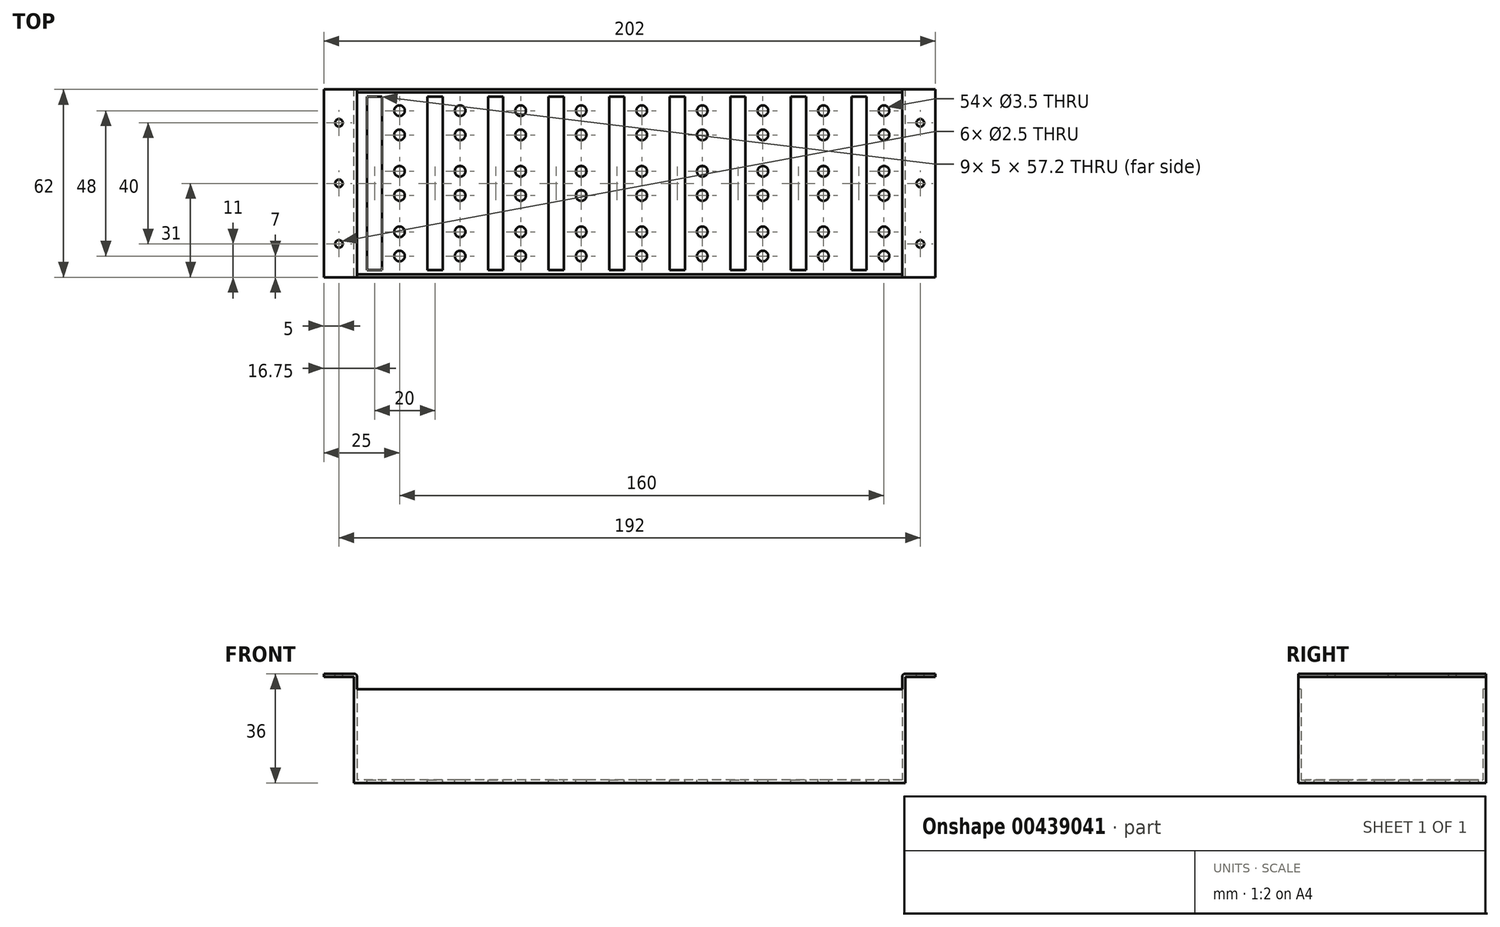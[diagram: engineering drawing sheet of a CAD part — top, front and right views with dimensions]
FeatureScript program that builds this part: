
annotation { "Feature Type Name" : "Feature", "Feature Type Description" : "" }
export const myFeature = defineFeature(function(context is Context, id is Id, definition is map)
    precondition{}
    {
        {
            var Q0;
            Q0=qCreatedBy(makeId("Top.planeOp"),FACE);
            var sketch = newSketch(context, id + "F0", { "sketchPlane" : qUnion([Q0])});
            skLineSegment(sketch, "E0.bottom", {"start": v(91, -31) * mm, "end": v(-91, -31) * mm});
            skLineSegment(sketch, "E0.top", {"start": v(91, 31) * mm, "end": v(-91, 31) * mm});
            skLineSegment(sketch, "E0.left", {"start": v(91, -31) * mm, "end": v(91, 31) * mm});
            skLineSegment(sketch, "E0.right", {"start": v(-91, -31) * mm, "end": v(-91, 31) * mm});
            skPoint(sketch, "E0.middle", {"position": v(0, 0) * mm});
            skSolve(sketch);
        }
        {
            var Q0;
            Q0=qSketchRegion(id+"F0",true);
            extrude(context, id + "F1", {"entities" : qUnion([Q0]), "depth" : 36 * mm});
        }
        {
            var Q0;
            Q0=makeQuery(id+"F1.opExtrude","CAP_FACE",FACE,{"disambiguationData":[OSD([sQuery(id+"F0.wireOp",EDGE,"E0.bottom"),sQuery(id+"F0.wireOp",EDGE,"E0.top"),sQuery(id+"F0.wireOp",EDGE,"E0.left"),sQuery(id+"F0.wireOp",EDGE,"E0.right")])],"isStart":false});
            shell(context, id + "F2", {"entities" : qUnion([Q0]), "thickness" : 1 * mm});
        }
        {
            var Q0;
            Q0=makeQuery(id+"F1.opExtrude","CAP_FACE",FACE,{"disambiguationData":[OSD([sQuery(id+"F0.wireOp",EDGE,"E0.bottom"),sQuery(id+"F0.wireOp",EDGE,"E0.top"),sQuery(id+"F0.wireOp",EDGE,"E0.left"),sQuery(id+"F0.wireOp",EDGE,"E0.right")])],"isStart":false});
            var sketch = newSketch(context, id + "F3", { "sketchPlane" : qUnion([Q0])});
            skLineSegment(sketch, "E1.bottom", {"start": v(-91, 31) * mm, "end": v(-101, 31) * mm});
            skLineSegment(sketch, "E1.top", {"start": v(-91, -31) * mm, "end": v(-101, -31) * mm});
            skLineSegment(sketch, "E1.left", {"start": v(-91, 31) * mm, "end": v(-91, -31) * mm});
            skLineSegment(sketch, "E1.right", {"start": v(-101, 31) * mm, "end": v(-101, -31) * mm});
            skCircle(sketch, "E2", {"center": v(-96, 20) * mm, "radius": 1.25 * mm});
            skCircle(sketch, "E3", {"center": v(-96, 0) * mm, "radius": 1.25 * mm});
            skCircle(sketch, "E4", {"center": v(-96, -20) * mm, "radius": 1.25 * mm});
            skCircle(sketch, "E5.MirrorC", {"center": v(96, 20) * mm, "radius": 1.25 * mm});
            skCircle(sketch, "E6.MirrorC", {"center": v(96, 0) * mm, "radius": 1.25 * mm});
            skCircle(sketch, "E7.MirrorC", {"center": v(96, -20) * mm, "radius": 1.25 * mm});
            skLineSegment(sketch, "E8.MirrorCS", {"start": v(91, 31) * mm, "end": v(101, 31) * mm});
            skLineSegment(sketch, "E9.MirrorCS", {"start": v(91, -31) * mm, "end": v(101, -31) * mm});
            skLineSegment(sketch, "E10.MirrorCS", {"start": v(91, 31) * mm, "end": v(91, -31) * mm});
            skLineSegment(sketch, "E11.MirrorCS", {"start": v(101, 31) * mm, "end": v(101, -31) * mm});
            skSolve(sketch);
        }
        {
            var Q0;
            Q0=qSketchRegion(id+"F3",true);
            extrude(context, id + "F4", {"entities" : qUnion([Q0]), "operationType" : NewBodyOperationType.ADD, "oppositeDirection" : true, "depth" : 1 * mm});
        }
        {
            var Q0;
            Q0=makeQuery(id+"F4.boolean.opBoolean","MERGE",FACE,{"derivedFrom":[makeQuery(id+"F1.opExtrude","SWEPT_FACE",FACE,{"disambiguationData":[OSD([sQuery(id+"F0.wireOp",EDGE,"E0.bottom")])]}),makeQuery(id+"F4.opExtrude","SWEPT_FACE",FACE,{"disambiguationData":[OSD([sQuery(id+"F3.wireOp",EDGE,"E1.top")])]}),makeQuery(id+"F4.opExtrude","SWEPT_FACE",FACE,{"disambiguationData":[OSD([sQuery(id+"F3.wireOp",EDGE,"E9.MirrorCS")])]})]});
            var sketch = newSketch(context, id + "F5", { "sketchPlane" : qUnion([Q0])});
            skLineSegment(sketch, "E12.bottom", {"start": v(-90, 39.58) * mm, "end": v(90, 39.58) * mm});
            skLineSegment(sketch, "E12.top", {"start": v(-90, 30.9) * mm, "end": v(90, 30.9) * mm});
            skLineSegment(sketch, "E12.left", {"start": v(-90, 39.58) * mm, "end": v(-90, 30.9) * mm});
            skLineSegment(sketch, "E12.right", {"start": v(90, 39.58) * mm, "end": v(90, 30.9) * mm});
            skSolve(sketch);
        }
        {
            var Q0;
            Q0=qSketchRegion(id+"F5",true);
            extrude(context, id + "F6", {"entities" : qUnion([Q0]), "operationType" : NewBodyOperationType.REMOVE, "oppositeDirection" : true, "depth" : 70 * mm});
        }
        {
            var Q0;
            Q0=makeQuery(id+"F6.boolean.opBoolean","INTERSECT",EDGE,{"derivedFrom":[makeQuery(id+"F4.boolean.opBoolean","MERGE",FACE,{"derivedFrom":[makeQuery(id+"F1.opExtrude","CAP_FACE",FACE,{"disambiguationData":[OSD([sQuery(id+"F0.wireOp",EDGE,"E0.bottom"),sQuery(id+"F0.wireOp",EDGE,"E0.top"),sQuery(id+"F0.wireOp",EDGE,"E0.left"),sQuery(id+"F0.wireOp",EDGE,"E0.right")])],"isStart":false}),makeQuery(id+"F4.opExtrude","CAP_FACE",FACE,{"disambiguationData":[OSD([sQuery(id+"F3.wireOp",EDGE,"E1.bottom"),sQuery(id+"F3.wireOp",EDGE,"E1.top"),sQuery(id+"F3.wireOp",EDGE,"E1.left"),sQuery(id+"F3.wireOp",EDGE,"E1.right"),sQuery(id+"F3.wireOp",EDGE,"E2"),sQuery(id+"F3.wireOp",EDGE,"E3"),sQuery(id+"F3.wireOp",EDGE,"E4")])],"isStart":true}),makeQuery(id+"F4.opExtrude","CAP_FACE",FACE,{"disambiguationData":[OSD([sQuery(id+"F3.wireOp",EDGE,"E5.MirrorC"),sQuery(id+"F3.wireOp",EDGE,"E6.MirrorC"),sQuery(id+"F3.wireOp",EDGE,"E7.MirrorC"),sQuery(id+"F3.wireOp",EDGE,"E8.MirrorCS"),sQuery(id+"F3.wireOp",EDGE,"E9.MirrorCS"),sQuery(id+"F3.wireOp",EDGE,"E10.MirrorCS"),sQuery(id+"F3.wireOp",EDGE,"E11.MirrorCS")])],"isStart":true})]}),makeQuery(id+"F6.opExtrude","SWEPT_FACE",FACE,{"disambiguationData":[OSD([sQuery(id+"F5.wireOp",EDGE,"E12.left")])]})]});
            var Q1;
            Q1=makeQuery(id+"F4.opExtrude","CAP_EDGE",EDGE,{"disambiguationData":[OSD([sQuery(id+"F3.wireOp",EDGE,"E1.left")])],"isStart":false});
            var Q2;
            Q2=makeQuery(id+"F6.boolean.opBoolean","INTERSECT",EDGE,{"derivedFrom":[makeQuery(id+"F4.boolean.opBoolean","MERGE",FACE,{"derivedFrom":[makeQuery(id+"F1.opExtrude","CAP_FACE",FACE,{"disambiguationData":[OSD([sQuery(id+"F0.wireOp",EDGE,"E0.bottom"),sQuery(id+"F0.wireOp",EDGE,"E0.top"),sQuery(id+"F0.wireOp",EDGE,"E0.left"),sQuery(id+"F0.wireOp",EDGE,"E0.right")])],"isStart":false}),makeQuery(id+"F4.opExtrude","CAP_FACE",FACE,{"disambiguationData":[OSD([sQuery(id+"F3.wireOp",EDGE,"E1.bottom"),sQuery(id+"F3.wireOp",EDGE,"E1.top"),sQuery(id+"F3.wireOp",EDGE,"E1.left"),sQuery(id+"F3.wireOp",EDGE,"E1.right"),sQuery(id+"F3.wireOp",EDGE,"E2"),sQuery(id+"F3.wireOp",EDGE,"E3"),sQuery(id+"F3.wireOp",EDGE,"E4")])],"isStart":true}),makeQuery(id+"F4.opExtrude","CAP_FACE",FACE,{"disambiguationData":[OSD([sQuery(id+"F3.wireOp",EDGE,"E5.MirrorC"),sQuery(id+"F3.wireOp",EDGE,"E6.MirrorC"),sQuery(id+"F3.wireOp",EDGE,"E7.MirrorC"),sQuery(id+"F3.wireOp",EDGE,"E8.MirrorCS"),sQuery(id+"F3.wireOp",EDGE,"E9.MirrorCS"),sQuery(id+"F3.wireOp",EDGE,"E10.MirrorCS"),sQuery(id+"F3.wireOp",EDGE,"E11.MirrorCS")])],"isStart":true})]}),makeQuery(id+"F6.opExtrude","SWEPT_FACE",FACE,{"disambiguationData":[OSD([sQuery(id+"F5.wireOp",EDGE,"E12.right")])]})]});
            var Q3;
            Q3=makeQuery(id+"F4.opExtrude","CAP_EDGE",EDGE,{"disambiguationData":[OSD([sQuery(id+"F3.wireOp",EDGE,"E10.MirrorCS")])],"isStart":false});
            fillet(context, id + "F7", {"entities" : qUnion([Q0, Q1, Q2, Q3]), "radius" : 1 * mm, "tangentPropagation" : true, "allowEdgeOverflow" : false});
        }
        {
            var Q0;
            Q0=makeQuery(id+"F2.opShell","OFFSET_FACE",FACE,{"disambiguationData":[OSD([sQuery(id+"F0.wireOp",EDGE,"E0.bottom"),sQuery(id+"F0.wireOp",EDGE,"E0.top"),sQuery(id+"F0.wireOp",EDGE,"E0.left"),sQuery(id+"F0.wireOp",EDGE,"E0.right")])]});
            var sketch = newSketch(context, id + "F8", { "sketchPlane" : qUnion([Q0])});
            skCircle(sketch, "E13", {"center": v(-76, 24) * mm, "radius": 1.75 * mm});
            skCircle(sketch, "E14", {"center": v(-76, 16) * mm, "radius": 1.75 * mm});
            skCircle(sketch, "E15.0.1.0", {"center": v(-76, 4) * mm, "radius": 1.75 * mm});
            skCircle(sketch, "E15.0.1.1", {"center": v(-76, -4) * mm, "radius": 1.75 * mm});
            skCircle(sketch, "E15.0.2.0", {"center": v(-76, -16) * mm, "radius": 1.75 * mm});
            skCircle(sketch, "E15.0.2.1", {"center": v(-76, -24) * mm, "radius": 1.75 * mm});
            skCircle(sketch, "E15.1.0.0", {"center": v(-56, 24) * mm, "radius": 1.75 * mm});
            skCircle(sketch, "E15.1.0.1", {"center": v(-56, 16) * mm, "radius": 1.75 * mm});
            skCircle(sketch, "E15.1.1.0", {"center": v(-56, 4) * mm, "radius": 1.75 * mm});
            skCircle(sketch, "E15.1.1.1", {"center": v(-56, -4) * mm, "radius": 1.75 * mm});
            skCircle(sketch, "E15.1.2.0", {"center": v(-56, -16) * mm, "radius": 1.75 * mm});
            skCircle(sketch, "E15.1.2.1", {"center": v(-56, -24) * mm, "radius": 1.75 * mm});
            skCircle(sketch, "E15.2.0.0", {"center": v(-36, 24) * mm, "radius": 1.75 * mm});
            skCircle(sketch, "E15.2.0.1", {"center": v(-36, 16) * mm, "radius": 1.75 * mm});
            skCircle(sketch, "E15.2.1.0", {"center": v(-36, 4) * mm, "radius": 1.75 * mm});
            skCircle(sketch, "E15.2.1.1", {"center": v(-36, -4) * mm, "radius": 1.75 * mm});
            skCircle(sketch, "E15.2.2.0", {"center": v(-36, -16) * mm, "radius": 1.75 * mm});
            skCircle(sketch, "E15.2.2.1", {"center": v(-36, -24) * mm, "radius": 1.75 * mm});
            skCircle(sketch, "E15.3.0.0", {"center": v(-16, 24) * mm, "radius": 1.75 * mm});
            skCircle(sketch, "E15.3.0.1", {"center": v(-16, 16) * mm, "radius": 1.75 * mm});
            skCircle(sketch, "E15.3.1.0", {"center": v(-16, 4) * mm, "radius": 1.75 * mm});
            skCircle(sketch, "E15.3.1.1", {"center": v(-16, -4) * mm, "radius": 1.75 * mm});
            skCircle(sketch, "E15.3.2.0", {"center": v(-16, -16) * mm, "radius": 1.75 * mm});
            skCircle(sketch, "E15.3.2.1", {"center": v(-16, -24) * mm, "radius": 1.75 * mm});
            skCircle(sketch, "E15.4.0.0", {"center": v(4, 24) * mm, "radius": 1.75 * mm});
            skCircle(sketch, "E15.4.0.1", {"center": v(4, 16) * mm, "radius": 1.75 * mm});
            skCircle(sketch, "E15.4.1.0", {"center": v(4, 4) * mm, "radius": 1.75 * mm});
            skCircle(sketch, "E15.4.1.1", {"center": v(4, -4) * mm, "radius": 1.75 * mm});
            skCircle(sketch, "E15.4.2.0", {"center": v(4, -16) * mm, "radius": 1.75 * mm});
            skCircle(sketch, "E15.4.2.1", {"center": v(4, -24) * mm, "radius": 1.75 * mm});
            skCircle(sketch, "E15.5.0.0", {"center": v(24, 24) * mm, "radius": 1.75 * mm});
            skCircle(sketch, "E15.5.0.1", {"center": v(24, 16) * mm, "radius": 1.75 * mm});
            skCircle(sketch, "E15.5.1.0", {"center": v(24, 4) * mm, "radius": 1.75 * mm});
            skCircle(sketch, "E15.5.1.1", {"center": v(24, -4) * mm, "radius": 1.75 * mm});
            skCircle(sketch, "E15.5.2.0", {"center": v(24, -16) * mm, "radius": 1.75 * mm});
            skCircle(sketch, "E15.5.2.1", {"center": v(24, -24) * mm, "radius": 1.75 * mm});
            skCircle(sketch, "E15.6.0.0", {"center": v(44, 24) * mm, "radius": 1.75 * mm});
            skCircle(sketch, "E15.6.0.1", {"center": v(44, 16) * mm, "radius": 1.75 * mm});
            skCircle(sketch, "E15.6.1.0", {"center": v(44, 4) * mm, "radius": 1.75 * mm});
            skCircle(sketch, "E15.6.1.1", {"center": v(44, -4) * mm, "radius": 1.75 * mm});
            skCircle(sketch, "E15.6.2.0", {"center": v(44, -16) * mm, "radius": 1.75 * mm});
            skCircle(sketch, "E15.6.2.1", {"center": v(44, -24) * mm, "radius": 1.75 * mm});
            skCircle(sketch, "E15.7.0.0", {"center": v(64, 24) * mm, "radius": 1.75 * mm});
            skCircle(sketch, "E15.7.0.1", {"center": v(64, 16) * mm, "radius": 1.75 * mm});
            skCircle(sketch, "E15.7.1.0", {"center": v(64, 4) * mm, "radius": 1.75 * mm});
            skCircle(sketch, "E15.7.1.1", {"center": v(64, -4) * mm, "radius": 1.75 * mm});
            skCircle(sketch, "E15.7.2.0", {"center": v(64, -16) * mm, "radius": 1.75 * mm});
            skCircle(sketch, "E15.7.2.1", {"center": v(64, -24) * mm, "radius": 1.75 * mm});
            skCircle(sketch, "E15.8.0.0", {"center": v(84, 24) * mm, "radius": 1.75 * mm});
            skCircle(sketch, "E15.8.0.1", {"center": v(84, 16) * mm, "radius": 1.75 * mm});
            skCircle(sketch, "E15.8.1.0", {"center": v(84, 4) * mm, "radius": 1.75 * mm});
            skCircle(sketch, "E15.8.1.1", {"center": v(84, -4) * mm, "radius": 1.75 * mm});
            skCircle(sketch, "E15.8.2.0", {"center": v(84, -16) * mm, "radius": 1.75 * mm});
            skCircle(sketch, "E15.8.2.1", {"center": v(84, -24) * mm, "radius": 1.75 * mm});
            skLineSegment(sketch, "E15.direction1", {"start": v(-76, 24) * mm, "end": v(-56, 24) * mm, "construction": true});
            skLineSegment(sketch, "E15.direction2", {"start": v(-76, 24) * mm, "end": v(-76, 4) * mm, "construction": true});
            skLineSegment(sketch, "E16.bottom", {"start": v(-86.75, 28.6) * mm, "end": v(-81.75, 28.6) * mm});
            skLineSegment(sketch, "E16.top", {"start": v(-86.75, -28.6) * mm, "end": v(-81.75, -28.6) * mm});
            skLineSegment(sketch, "E16.left", {"start": v(-86.75, 28.6) * mm, "end": v(-86.75, -28.6) * mm});
            skLineSegment(sketch, "E16.right", {"start": v(-81.75, 28.6) * mm, "end": v(-81.75, -28.6) * mm});
            skLineSegment(sketch, "E17.1.0.0", {"start": v(-66.75, 28.6) * mm, "end": v(-66.75, -28.6) * mm});
            skLineSegment(sketch, "E17.1.0.1", {"start": v(-66.75, -28.6) * mm, "end": v(-61.75, -28.6) * mm});
            skLineSegment(sketch, "E17.1.0.2", {"start": v(-66.75, 28.6) * mm, "end": v(-61.75, 28.6) * mm});
            skLineSegment(sketch, "E17.1.0.3", {"start": v(-61.75, 28.6) * mm, "end": v(-61.75, -28.6) * mm});
            skLineSegment(sketch, "E17.2.0.0", {"start": v(-46.75, 28.6) * mm, "end": v(-46.75, -28.6) * mm});
            skLineSegment(sketch, "E17.2.0.1", {"start": v(-46.75, -28.6) * mm, "end": v(-41.75, -28.6) * mm});
            skLineSegment(sketch, "E17.2.0.2", {"start": v(-46.75, 28.6) * mm, "end": v(-41.75, 28.6) * mm});
            skLineSegment(sketch, "E17.2.0.3", {"start": v(-41.75, 28.6) * mm, "end": v(-41.75, -28.6) * mm});
            skLineSegment(sketch, "E17.3.0.0", {"start": v(-26.75, 28.6) * mm, "end": v(-26.75, -28.6) * mm});
            skLineSegment(sketch, "E17.3.0.1", {"start": v(-26.75, -28.6) * mm, "end": v(-21.75, -28.6) * mm});
            skLineSegment(sketch, "E17.3.0.2", {"start": v(-26.75, 28.6) * mm, "end": v(-21.75, 28.6) * mm});
            skLineSegment(sketch, "E17.3.0.3", {"start": v(-21.75, 28.6) * mm, "end": v(-21.75, -28.6) * mm});
            skLineSegment(sketch, "E17.4.0.0", {"start": v(-6.75, 28.6) * mm, "end": v(-6.75, -28.6) * mm});
            skLineSegment(sketch, "E17.4.0.1", {"start": v(-6.75, -28.6) * mm, "end": v(-1.75, -28.6) * mm});
            skLineSegment(sketch, "E17.4.0.2", {"start": v(-6.75, 28.6) * mm, "end": v(-1.75, 28.6) * mm});
            skLineSegment(sketch, "E17.4.0.3", {"start": v(-1.75, 28.6) * mm, "end": v(-1.75, -28.6) * mm});
            skLineSegment(sketch, "E17.5.0.0", {"start": v(13.25, 28.6) * mm, "end": v(13.25, -28.6) * mm});
            skLineSegment(sketch, "E17.5.0.1", {"start": v(13.25, -28.6) * mm, "end": v(18.25, -28.6) * mm});
            skLineSegment(sketch, "E17.5.0.2", {"start": v(13.25, 28.6) * mm, "end": v(18.25, 28.6) * mm});
            skLineSegment(sketch, "E17.5.0.3", {"start": v(18.25, 28.6) * mm, "end": v(18.25, -28.6) * mm});
            skLineSegment(sketch, "E17.6.0.0", {"start": v(33.25, 28.6) * mm, "end": v(33.25, -28.6) * mm});
            skLineSegment(sketch, "E17.6.0.1", {"start": v(33.25, -28.6) * mm, "end": v(38.25, -28.6) * mm});
            skLineSegment(sketch, "E17.6.0.2", {"start": v(33.25, 28.6) * mm, "end": v(38.25, 28.6) * mm});
            skLineSegment(sketch, "E17.6.0.3", {"start": v(38.25, 28.6) * mm, "end": v(38.25, -28.6) * mm});
            skLineSegment(sketch, "E17.7.0.0", {"start": v(53.25, 28.6) * mm, "end": v(53.25, -28.6) * mm});
            skLineSegment(sketch, "E17.7.0.1", {"start": v(53.25, -28.6) * mm, "end": v(58.25, -28.6) * mm});
            skLineSegment(sketch, "E17.7.0.2", {"start": v(53.25, 28.6) * mm, "end": v(58.25, 28.6) * mm});
            skLineSegment(sketch, "E17.7.0.3", {"start": v(58.25, 28.6) * mm, "end": v(58.25, -28.6) * mm});
            skLineSegment(sketch, "E17.8.0.0", {"start": v(73.25, 28.6) * mm, "end": v(73.25, -28.6) * mm});
            skLineSegment(sketch, "E17.8.0.1", {"start": v(73.25, -28.6) * mm, "end": v(78.25, -28.6) * mm});
            skLineSegment(sketch, "E17.8.0.2", {"start": v(73.25, 28.6) * mm, "end": v(78.25, 28.6) * mm});
            skLineSegment(sketch, "E17.8.0.3", {"start": v(78.25, 28.6) * mm, "end": v(78.25, -28.6) * mm});
            skLineSegment(sketch, "E17.direction1", {"start": v(-86.75, -28.6) * mm, "end": v(-66.75, -28.6) * mm, "construction": true});
            skSolve(sketch);
        }
        {
            var Q0;
            Q0=qSketchRegion(id+"F8",true);
            extrude(context, id + "F9", {"entities" : qUnion([Q0]), "operationType" : NewBodyOperationType.REMOVE, "oppositeDirection" : true, "depth" : 25 * mm});
        }
    });
